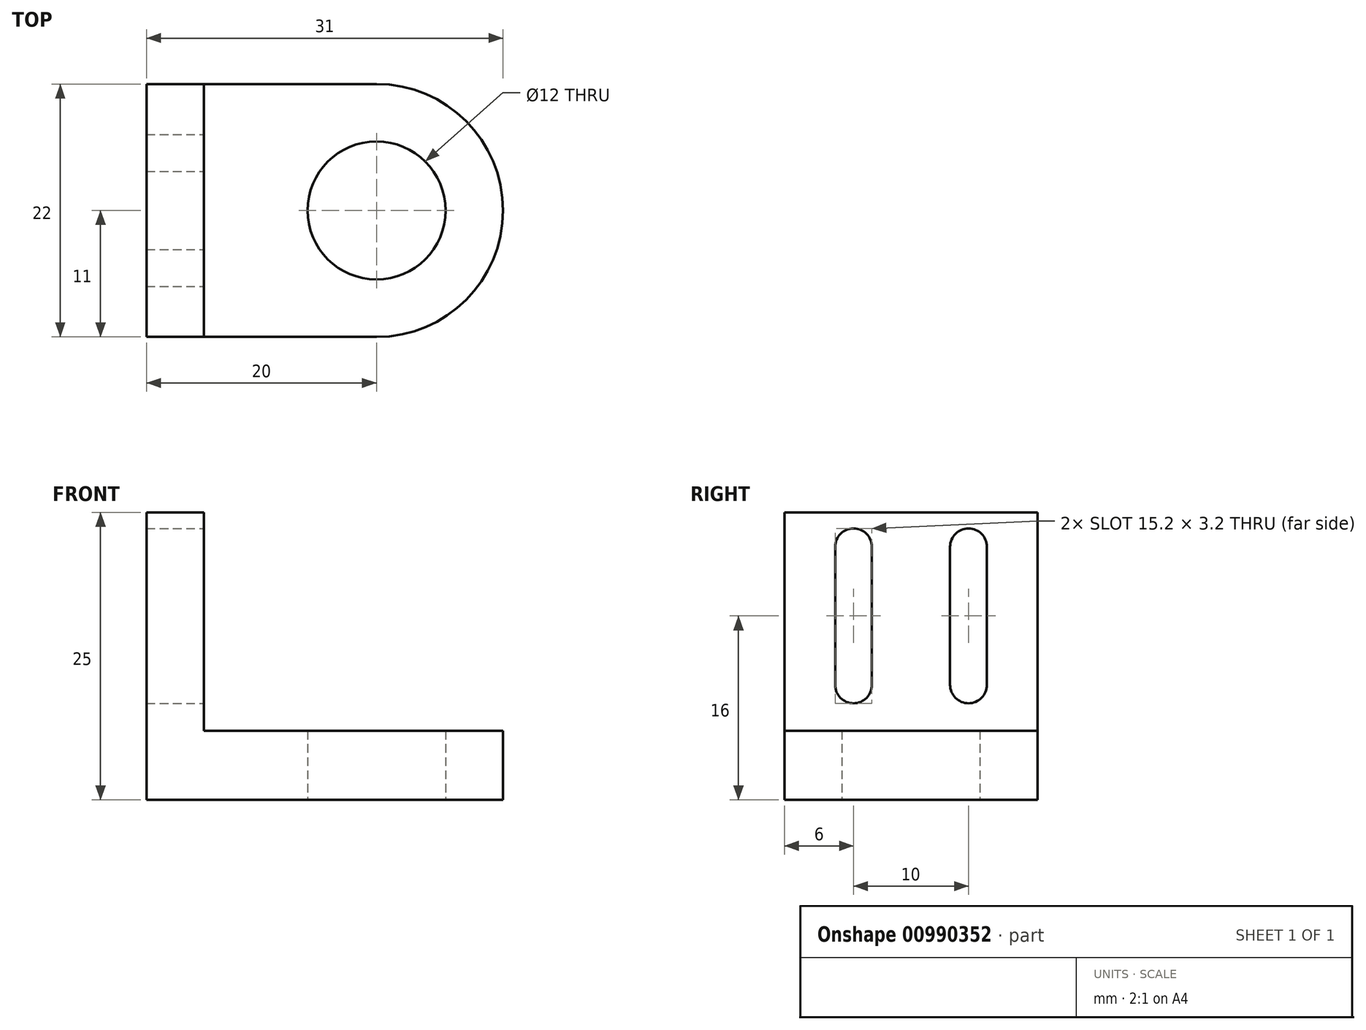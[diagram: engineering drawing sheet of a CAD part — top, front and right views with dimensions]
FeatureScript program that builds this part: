
annotation { "Feature Type Name" : "Feature", "Feature Type Description" : "" }
export const myFeature = defineFeature(function(context is Context, id is Id, definition is map)
    precondition{}
    {
        {
            var Q0;
            Q0=qCreatedBy(makeId("Top.planeOp"),FACE);
            var sketch = newSketch(context, id + "F0", { "sketchPlane" : qUnion([Q0])});
            skCircle(sketch, "E0", {"center": v(0, 0) * mm, "radius": 6 * mm});
            skCircle(sketch, "E1", {"center": v(0, 0) * mm, "radius": 11 * mm});
            skLineSegment(sketch, "E2", {"start": v(0, -11) * mm, "end": v(-15, -11) * mm});
            skLineSegment(sketch, "E3", {"start": v(0, 11) * mm, "end": v(-15, 11) * mm});
            skLineSegment(sketch, "E4", {"start": v(-15, 11) * mm, "end": v(-15, -11) * mm});
            skSolve(sketch);
        }
        {
            var Q0;
            {var subQ0=sQuery(id+"F0.wireOp",EDGE,"E2");Q0=makeQuery(id+"F0.imprint","IMPRINT",FACE,{"disambiguationData":[TD([[makeQuery(id+"F0.imprint","IMPRINT",EDGE,{"derivedFrom":subQ0}),-1.0]])]});}
            var Q1;
            Q1=makeQuery(id+"F0.imprint","IMPRINT",FACE,{"disambiguationData":[TD([[makeQuery(id+"F0.imprint","IMPRINT",EDGE,{"derivedFrom":sQuery(id+"F0.wireOp",EDGE,"E0")}),-1.0]])]});
            extrude(context, id + "F1", {"entities" : qUnion([Q0, Q1]), "depth" : 6 * mm, "offsetDistance" : 25 * mm});
        }
        {
            var Q0;
            Q0=makeQuery(id+"F1.opExtrude","SWEPT_FACE",FACE,{"disambiguationData":[OSD([sQuery(id+"F0.wireOp",EDGE,"E4")])]});
            var sketch = newSketch(context, id + "F2", { "sketchPlane" : qUnion([Q0])});
            skLineSegment(sketch, "E5", {"start": v(0, 0) * mm, "end": v(0, 25) * mm, "construction": true});
            skLineSegment(sketch, "E6", {"start": v(5, 25) * mm, "end": v(5, 0) * mm, "construction": true});
            skLineSegment(sketch, "E7", {"start": v(-5, 25) * mm, "end": v(-5, 0) * mm, "construction": true});
            skLineSegment(sketch, "E8.bottom", {"start": v(-11, 0) * mm, "end": v(11, 0) * mm});
            skLineSegment(sketch, "E8.top", {"start": v(-11, 25) * mm, "end": v(11, 25) * mm});
            skLineSegment(sketch, "E8.left", {"start": v(-11, 0) * mm, "end": v(-11, 25) * mm});
            skLineSegment(sketch, "E8.right", {"start": v(11, 0) * mm, "end": v(11, 25) * mm});
            skLineSegment(sketch, "E9.left", {"start": v(-3.4, 10) * mm, "end": v(-3.4, 22) * mm});
            skLineSegment(sketch, "E9.right", {"start": v(-6.6, 10) * mm, "end": v(-6.6, 22) * mm});
            skPoint(sketch, "E9.middle", {"position": v(-5, 16) * mm});
            skArc(sketch, "E10", {"start": v(-3.4, 22) * mm, "mid": v(-5, 23.6) * mm, "end": v(-6.6, 22) * mm});
            skArc(sketch, "E11", {"start": v(-6.6, 10) * mm, "mid": v(-5, 8.4) * mm, "end": v(-3.4, 10) * mm});
            skLineSegment(sketch, "E12.MirrorCS", {"start": v(6.6, 10) * mm, "end": v(6.6, 22) * mm});
            skLineSegment(sketch, "E13.MirrorCS", {"start": v(3.4, 10) * mm, "end": v(3.4, 22) * mm});
            skArc(sketch, "E14.MirrorCS", {"start": v(6.6, 10) * mm, "mid": v(5, 8.4) * mm, "end": v(3.4, 10) * mm});
            skArc(sketch, "E15.MirrorCS", {"start": v(3.4, 22) * mm, "mid": v(5, 23.6) * mm, "end": v(6.6, 22) * mm});
            skSolve(sketch);
        }
        {
            var Q0;
            {var subQ0=sQuery(id+"F2.wireOp",EDGE,"E8.top");Q0=makeQuery(id+"F2.imprint","IMPRINT",FACE,{"disambiguationData":[TD([[makeQuery(id+"F2.imprint","IMPRINT",EDGE,{"derivedFrom":subQ0}),-1.0]])]});}
            var Q1;
            {var subQ0=sQuery(id+"F2.wireOp",EDGE,"E8.bottom");Q1=makeQuery(id+"F2.imprint","IMPRINT",FACE,{"disambiguationData":[TD([[makeQuery(id+"F2.imprint","IMPRINT",EDGE,{"derivedFrom":subQ0}),1.0]])]});}
            extrude(context, id + "F3", {"entities" : qUnion([Q0, Q1]), "operationType" : NewBodyOperationType.ADD, "depth" : 5 * mm, "offsetDistance" : 25 * mm});
        }
    });
